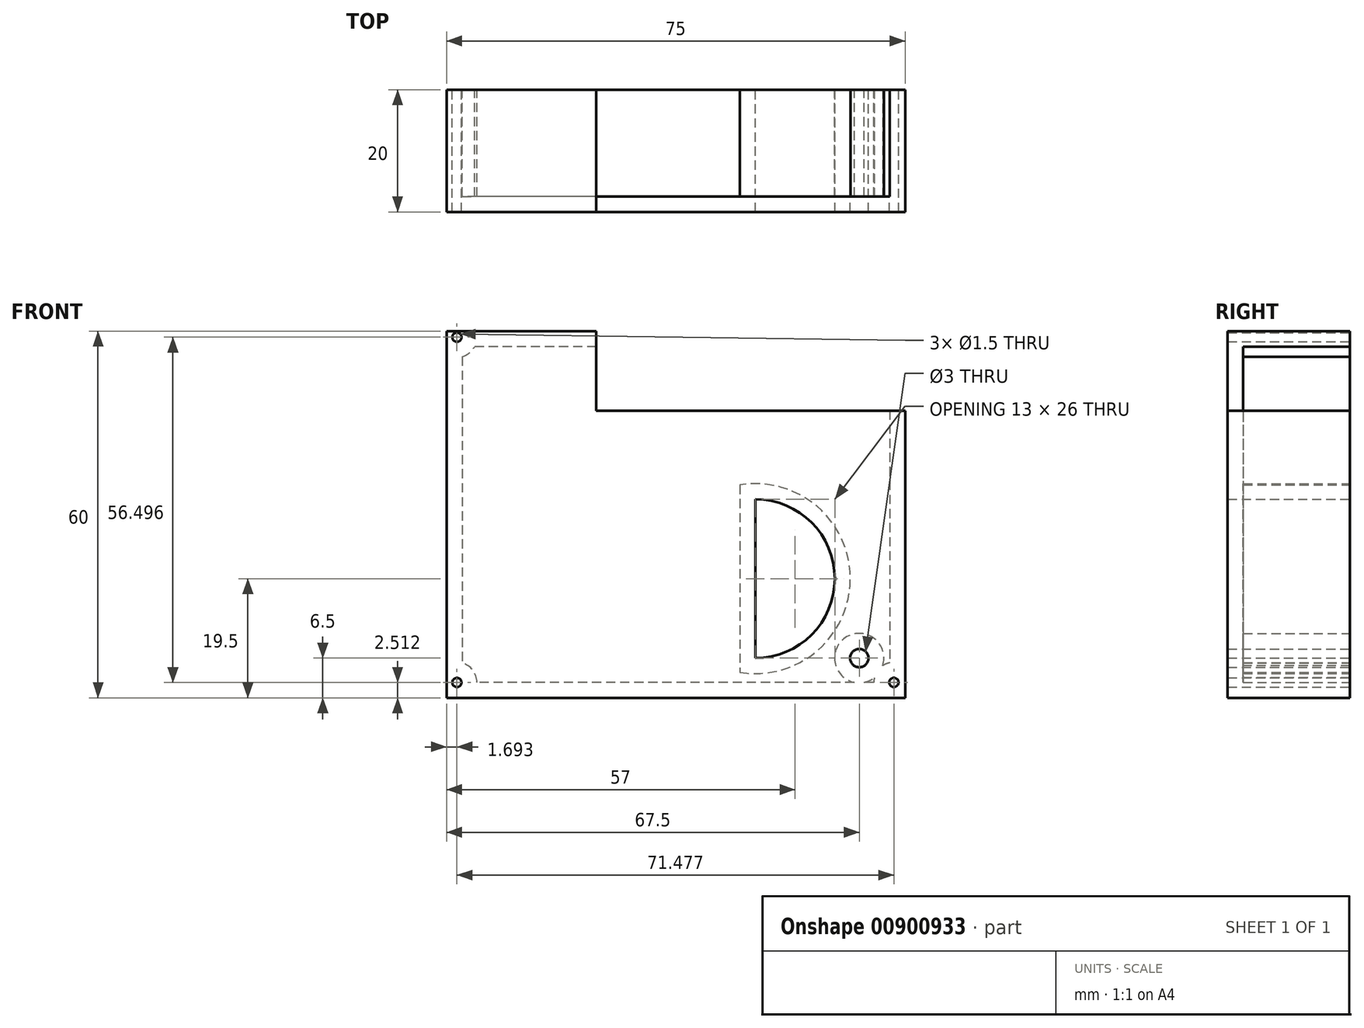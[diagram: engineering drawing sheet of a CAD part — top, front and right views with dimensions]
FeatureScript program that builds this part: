
annotation { "Feature Type Name" : "Feature", "Feature Type Description" : "" }
export const myFeature = defineFeature(function(context is Context, id is Id, definition is map)
    precondition{}
    {
        {
            var Q0;
            Q0=qCreatedBy(makeId("Front.planeOp"),FACE);
            var sketch = newSketch(context, id + "F0", { "sketchPlane" : qUnion([Q0])});
            skLineSegment(sketch, "E0.bottom", {"start": v(37.5, 29.18) * mm, "end": v(-37.5, 29.18) * mm});
            skLineSegment(sketch, "E0.top", {"start": v(37.5, -30.82) * mm, "end": v(-37.5, -30.82) * mm});
            skLineSegment(sketch, "E0.left", {"start": v(37.5, 29.18) * mm, "end": v(37.5, -30.82) * mm});
            skLineSegment(sketch, "E0.right", {"start": v(-37.5, 29.18) * mm, "end": v(-37.5, -30.82) * mm});
            skPoint(sketch, "E0.middle", {"position": v(0, -0.82) * mm});
            skLineSegment(sketch, "E1.bottom", {"start": v(-37.5, 29.18) * mm, "end": v(-36.55, 29.18) * mm});
            skLineSegment(sketch, "E1.left", {"start": v(-37.5, 29.18) * mm, "end": v(-37.5, -29.08) * mm});
            skLineSegment(sketch, "E2.bottom", {"start": v(-36.55, 29.18) * mm, "end": v(37.5, 29.18) * mm});
            skLineSegment(sketch, "E2.left", {"start": v(-36.55, 29.18) * mm, "end": v(-36.55, 28.18) * mm});
            skLineSegment(sketch, "E2.right", {"start": v(37.5, 29.18) * mm, "end": v(37.5, 28.18) * mm});
            skCircle(sketch, "E3", {"center": v(-35.8, 28.19) * mm, "radius": 0.75 * mm});
            skCircle(sketch, "E4", {"center": v(35.67, 28.18) * mm, "radius": 0.75 * mm});
            skLineSegment(sketch, "E5.bottom", {"start": v(-37.5, -30.82) * mm, "end": v(37.49, -30.82) * mm});
            skLineSegment(sketch, "E5.left", {"start": v(-37.5, -30.82) * mm, "end": v(-37.5, -29.82) * mm});
            skLineSegment(sketch, "E5.right", {"start": v(37.49, -30.82) * mm, "end": v(37.49, -29.82) * mm});
            skLineSegment(sketch, "E6.bottom", {"start": v(37.49, -29.82) * mm, "end": v(36.49, -29.82) * mm});
            skLineSegment(sketch, "E6.top", {"start": v(37.49, 28.9) * mm, "end": v(36.49, 28.9) * mm});
            skLineSegment(sketch, "E6.left", {"start": v(37.49, -29.82) * mm, "end": v(37.49, 28.9) * mm});
            skCircle(sketch, "E7", {"center": v(35.67, -28.3) * mm, "radius": 0.75 * mm});
            skCircle(sketch, "E8", {"center": v(-35.8, -28.3) * mm, "radius": 0.75 * mm});
            skLineSegment(sketch, "E9.bottom", {"start": v(-12.54, 29.18) * mm, "end": v(16.73, 29.18) * mm});
            skPoint(sketch, "E10", {"position": v(0, 21.18) * mm});
            skLineSegment(sketch, "E11.bottom", {"start": v(-13, 16.18) * mm, "end": v(13, 16.18) * mm});
            skLineSegment(sketch, "E11.top", {"start": v(-13, 26.18) * mm, "end": v(13, 26.18) * mm});
            skLineSegment(sketch, "E11.left", {"start": v(-13, 16.18) * mm, "end": v(-13, 26.18) * mm});
            skLineSegment(sketch, "E11.right", {"start": v(13, 16.18) * mm, "end": v(13, 26.18) * mm});
            skLineSegment(sketch, "E12.bottom", {"start": v(37.5, -30.82) * mm, "end": v(30, -30.82) * mm});
            skLineSegment(sketch, "E12.top", {"start": v(37.5, -24.32) * mm, "end": v(30, -24.32) * mm});
            skLineSegment(sketch, "E12.left", {"start": v(37.5, -30.82) * mm, "end": v(37.5, -24.32) * mm});
            skLineSegment(sketch, "E12.right", {"start": v(30, -30.82) * mm, "end": v(30, -24.32) * mm});
            skCircle(sketch, "E13", {"center": v(30, -24.32) * mm, "radius": 1.5 * mm});
            skLineSegment(sketch, "E14", {"start": v(13, 16.18) * mm, "end": v(37.5, 16.18) * mm});
            skLineSegment(sketch, "E15", {"start": v(-13, 26.18) * mm, "end": v(-13, 29.18) * mm});
            skLineSegment(sketch, "E16", {"start": v(13, 16.18) * mm, "end": v(13, -30.82) * mm});
            skLineSegment(sketch, "E17", {"start": v(30, -24.32) * mm, "end": v(13, -24.32) * mm});
            skLineSegment(sketch, "E18", {"start": v(13, -24.32) * mm, "end": v(13, 1.68) * mm});
            skArc(sketch, "E19.MirrorCS", {"start": v(13, -24.32) * mm, "mid": v(26, -11.32) * mm, "end": v(13, 1.68) * mm});
            skSolve(sketch);
        }
        {
            var Q0;
            {var subQ4=sQuery(id+"F0.wireOp",EDGE,"E5.right");Q0=makeQuery(id+"F0.imprint","IMPRINT",FACE,{"disambiguationData":[TD([[makeQuery(id+"F0.imprint","IMPRINT",EDGE,{"derivedFrom":subQ4}),-1.0]])]});}
            var Q1;
            {var subQ3=sQuery(id+"F0.wireOp",EDGE,"E14");var subQ5=sQuery(id+"F0.wireOp",EDGE,"E6.left");var subQ6=makeQuery(id+"F0.imprint","INTERSECT",VERTEX,{"derivedFrom":[subQ5,subQ3]});Q1=makeQuery(id+"F0.imprint","IMPRINT",FACE,{"disambiguationData":[TD([[makeQuery(id+"F0.imprint","IMPRINT",EDGE,{"disambiguationData":[TD([[subQ6,1.0]])],"derivedFrom":subQ5}),-1.0]])]});}
            var Q2;
            {var subQ5=sQuery(id+"F0.wireOp",EDGE,"E13");var subQ6=sQuery(id+"F0.wireOp",EDGE,"E12.right");var subQ7=makeQuery(id+"F0.imprint","INTERSECT",VERTEX,{"derivedFrom":[subQ6,subQ5]});Q2=makeQuery(id+"F0.imprint","IMPRINT",FACE,{"disambiguationData":[TD([[makeQuery(id+"F0.imprint","IMPRINT",EDGE,{"disambiguationData":[TD([[subQ7,1.0]])],"derivedFrom":subQ5}),-1.0]])]});}
            var Q3;
            {var subQ5=sQuery(id+"F0.wireOp",EDGE,"E2.right");Q3=makeQuery(id+"F0.imprint","IMPRINT",FACE,{"disambiguationData":[TD([[makeQuery(id+"F0.imprint","IMPRINT",EDGE,{"derivedFrom":subQ5}),-1.0]])]});}
            var Q4;
            {var subQ3=sQuery(id+"F0.wireOp",EDGE,"E5.right");Q4=makeQuery(id+"F0.imprint","IMPRINT",FACE,{"disambiguationData":[TD([[makeQuery(id+"F0.imprint","IMPRINT",EDGE,{"derivedFrom":subQ3}),1.0]])]});}
            var Q5;
            {var subQ10=sQuery(id+"F0.wireOp",EDGE,"E19.MirrorCS");Q5=makeQuery(id+"F0.imprint","IMPRINT",FACE,{"disambiguationData":[TD([[makeQuery(id+"F0.imprint","IMPRINT",EDGE,{"derivedFrom":subQ10}),-1.0]])]});}
            var Q6;
            Q6=makeQuery(id+"F0.imprint","IMPRINT",FACE,{"disambiguationData":[TD([[makeQuery(id+"F0.imprint","IMPRINT",EDGE,{"derivedFrom":sQuery(id+"F0.wireOp",EDGE,"E18")}),-1.0]])]});
            var Q7;
            Q7=makeQuery(id+"F0.imprint","IMPRINT",FACE,{"disambiguationData":[TD([[makeQuery(id+"F0.imprint","IMPRINT",EDGE,{"derivedFrom":sQuery(id+"F0.wireOp",EDGE,"E0.right")}),1.0]])]});
            extrude(context, id + "F1", {"entities" : qUnion([Q0, Q1, Q2, Q3, Q4, Q5, Q6, Q7]), "depth" : 20 * mm, "offsetDistance" : 25.4 * mm});
        }
        {
            var Q0;
            Q0=makeQuery(id+"F1.opExtrude","CAP_FACE",FACE,{"disambiguationData":[OSD([sQuery(id+"F0.wireOp",EDGE,"E0.left"),sQuery(id+"F0.wireOp",EDGE,"E0.right"),sQuery(id+"F0.wireOp",EDGE,"E1.bottom"),sQuery(id+"F0.wireOp",EDGE,"E1.left"),sQuery(id+"F0.wireOp",EDGE,"E2.bottom"),sQuery(id+"F0.wireOp",EDGE,"E2.right"),sQuery(id+"F0.wireOp",EDGE,"E3"),sQuery(id+"F0.wireOp",EDGE,"E4"),sQuery(id+"F0.wireOp",EDGE,"E5.bottom"),sQuery(id+"F0.wireOp",EDGE,"E5.left"),sQuery(id+"F0.wireOp",EDGE,"E7"),sQuery(id+"F0.wireOp",EDGE,"E8"),sQuery(id+"F0.wireOp",EDGE,"E9.bottom"),sQuery(id+"F0.wireOp",EDGE,"E11.bottom"),sQuery(id+"F0.wireOp",EDGE,"E11.top"),sQuery(id+"F0.wireOp",EDGE,"E11.left"),sQuery(id+"F0.wireOp",EDGE,"E11.right"),sQuery(id+"F0.wireOp",EDGE,"E12.bottom"),sQuery(id+"F0.wireOp",EDGE,"E12.left"),sQuery(id+"F0.wireOp",EDGE,"E13")])],"isStart":true});
            var Q1;
            Q1=makeQuery(id+"F1.opExtrude","SWEPT_FACE",FACE,{"disambiguationData":[OSD([sQuery(id+"F0.wireOp",EDGE,"E11.bottom")])]});
            var Q2;
            Q2=makeQuery(id+"F1.opExtrude","SWEPT_FACE",FACE,{"disambiguationData":[OSD([sQuery(id+"F0.wireOp",EDGE,"E11.right")])]});
            var Q3;
            Q3=makeQuery(id+"F1.opExtrude","SWEPT_FACE",FACE,{"disambiguationData":[OSD([sQuery(id+"F0.wireOp",EDGE,"E11.left")])]});
            var Q4;
            Q4=makeQuery(id+"F1.opExtrude","SWEPT_FACE",FACE,{"disambiguationData":[OSD([sQuery(id+"F0.wireOp",EDGE,"E11.top")])]});
            shell(context, id + "F2", {"entities" : qUnion([Q0, Q1, Q2, Q3, Q4]), "thickness" : 2.54 * mm});
        }
    });
